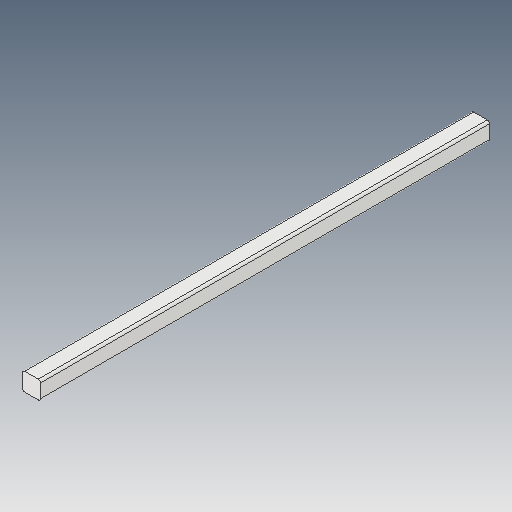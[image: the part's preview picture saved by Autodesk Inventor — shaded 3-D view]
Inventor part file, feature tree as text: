
AUTODESK INVENTOR PART (.ipt)
format: ipt  version: 2023.5 (Build 275446000, 446)  size: 86,016 bytes
history: native  units: in
note: dims shown in document units (in); Inventor stores cm internally (conversion verified against a paired STEP export)
features: fillet x1
ambient origin geometry x8: Origin, YZ Plane, XZ Plane, XY Plane, X Axis, Y Axis, Z Axis, Center Point
bodies: Solid1 (feature_tree)
feature tree (1):
  fillet  "Fillet1"  [1 undecoded]
note: 1 required parameter value undecoded (feature->parameter linkage not recoverable at this tier; creation-order binding heuristic only, values carry confidence <= 0.55)
